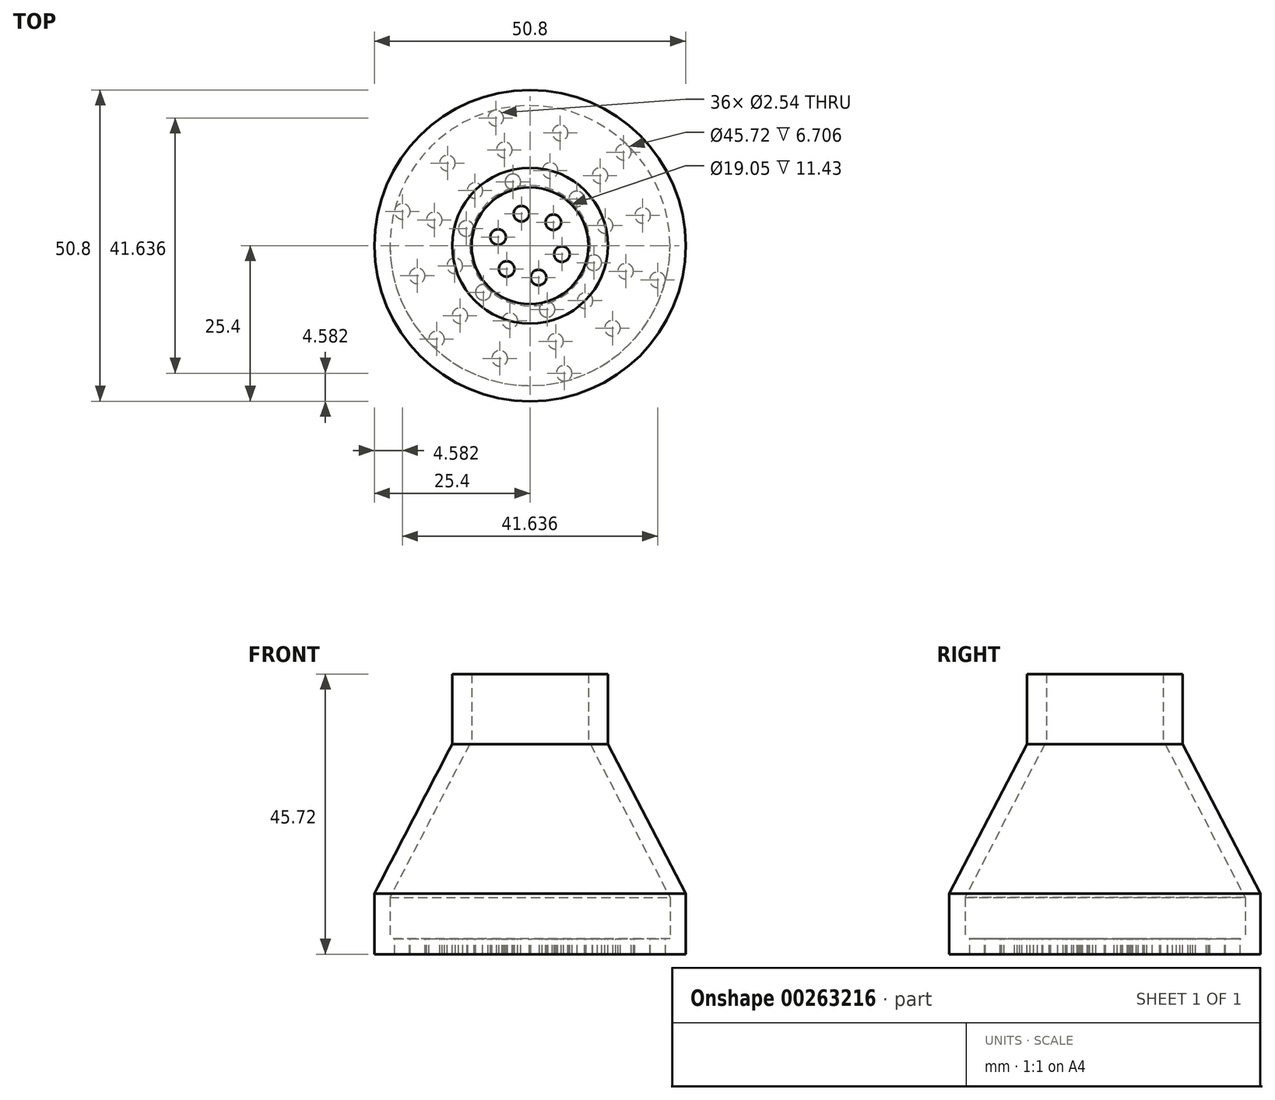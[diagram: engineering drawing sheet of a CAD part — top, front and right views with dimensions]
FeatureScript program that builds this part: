
annotation { "Feature Type Name" : "Feature", "Feature Type Description" : "" }
export const myFeature = defineFeature(function(context is Context, id is Id, definition is map)
    precondition{}
    {
        {
            var Q0;
            Q0=qCreatedBy(makeId("Top.planeOp"),FACE);
            var sketch = newSketch(context, id + "F0", { "sketchPlane" : qUnion([Q0])});
            skCircle(sketch, "E0", {"center": v(0, 0) * mm, "radius": 25.4 * mm});
            skSolve(sketch);
        }
        {
            var Q0;
            Q0 = qSketchRegion(id + "F0", true);
            var Q1;
            Q1=sQuery(id+"F0.wireOp",EDGE,"E0");
            extrude(context, id + "F1", {"entities" : qUnion([Q0]), "surfaceEntities" : qUnion([Q1]), "depth" : 31.75 * mm});
        }
        {
            var Q0;
            Q0=qCreatedBy(makeId("Right.planeOp"),FACE);
            var sketch = newSketch(context, id + "F2", { "sketchPlane" : qUnion([Q0])});
            skLineSegment(sketch, "E1", {"start": v(0, 0) * mm, "end": v(-29.21, 0) * mm, "construction": true});
            skLineSegment(sketch, "E2", {"start": v(-29.21, 0) * mm, "end": v(-12.7, 31.75) * mm});
            skLineSegment(sketch, "E3", {"start": v(-12.7, 31.75) * mm, "end": v(0, 31.75) * mm, "construction": true});
            skLineSegment(sketch, "E4", {"start": v(0, 31.75) * mm, "end": v(0, 0) * mm, "construction": true});
            skLineSegment(sketch, "E5", {"start": v(-29.21, 0) * mm, "end": v(-29.21, 31.75) * mm});
            skLineSegment(sketch, "E6", {"start": v(-29.21, 31.75) * mm, "end": v(-12.7, 31.75) * mm});
            skSolve(sketch);
        }
        {
            var Q0;
            Q0=makeQuery(id+"F2.imprint","IMPRINT",FACE,{"disambiguationData":[TD([[makeQuery(id+"F2.imprint","IMPRINT",EDGE,{"derivedFrom":sQuery(id+"F2.wireOp",EDGE,"E2")}),1.0]])]});
            var Q1;
            Q1=sQuery(id+"F2.wireOp",EDGE,"E4");
            revolve(context, id + "F3", {"operationType" : NewBodyOperationType.REMOVE, "entities" : qUnion([Q0]), "axis" : qUnion([Q1]), "revolveType" : RevolveType.FULL, "oppositeDirection" : true});
        }
        {
            var Q0;
            Q0=makeQuery(id+"F1.opExtrude","CAP_FACE",FACE,{"disambiguationData":[OSD([sQuery(id+"F0.wireOp",EDGE,"E0")])],"isStart":true});
            var Q1;
            Q1=makeQuery(id+"F1.opExtrude","CAP_FACE",FACE,{"disambiguationData":[OSD([sQuery(id+"F0.wireOp",EDGE,"E0")])],"isStart":false});
            shell(context, id + "F4", {"entities" : qUnion([Q0, Q1]), "thickness" : 2.54 * mm});
        }
        {
            var Q0;
            Q0=makeQuery(id+"F1.opExtrude","CAP_FACE",FACE,{"disambiguationData":[OSD([sQuery(id+"F0.wireOp",EDGE,"E0")])],"isStart":false});
            var sketch = newSketch(context, id + "F5", { "sketchPlane" : qUnion([Q0])});
            skCircle(sketch, "E7", {"center": v(0, 0) * mm, "radius": 12.7 * mm});
            skCircle(sketch, "E8", {"center": v(0, 0) * mm, "radius": 9.53 * mm});
            skSolve(sketch);
        }
        {
            var Q0;
            Q0 = qSketchRegion(id + "F5", true);
            extrude(context, id + "F6", {"entities" : qUnion([Q0]), "operationType" : NewBodyOperationType.ADD, "depth" : 11.43 * mm});
        }
        {
            var Q0;
            Q0=makeQuery(id+"F1.opExtrude","CAP_FACE",FACE,{"disambiguationData":[OSD([sQuery(id+"F0.wireOp",EDGE,"E0")])],"isStart":true});
            var sketch = newSketch(context, id + "F7", { "sketchPlane" : qUnion([Q0])});
            skCircle(sketch, "E9", {"center": v(0, 0) * mm, "radius": 25.4 * mm});
            skLineSegment(sketch, "E10.bottom", {"start": v(0, 0) * mm, "end": v(-3.8, 0) * mm, "construction": true});
            skLineSegment(sketch, "E10.top", {"start": v(0, 3.81) * mm, "end": v(-3.81, 3.8) * mm, "construction": true});
            skLineSegment(sketch, "E10.left", {"start": v(0, 0) * mm, "end": v(0, 3.81) * mm, "construction": true});
            skLineSegment(sketch, "E10.right", {"start": v(-3.8, 0) * mm, "end": v(-3.81, 3.8) * mm, "construction": true});
            skCircle(sketch, "E11", {"center": v(-3.81, 3.8) * mm, "radius": 1.27 * mm});
            skCircle(sketch, "E12.1.0", {"center": v(5.2, 1.4) * mm, "radius": 1.27 * mm});
            skCircle(sketch, "E12.2.0", {"center": v(-1.4, -5.2) * mm, "radius": 1.27 * mm});
            skLineSegment(sketch, "E12.anchor1", {"start": v(0, 0) * mm, "end": v(-3.81, 3.8) * mm, "construction": true});
            skLineSegment(sketch, "E12.anchor2", {"start": v(0, 0) * mm, "end": v(-1.4, -5.2) * mm, "construction": true});
            skLineSegment(sketch, "E13", {"start": v(0, 0) * mm, "end": v(5.2, 1.4) * mm, "construction": true});
            skLineSegment(sketch, "E14", {"start": v(0, 0) * mm, "end": v(1.4, 5.2) * mm, "construction": true});
            skCircle(sketch, "E15", {"center": v(1.4, 5.2) * mm, "radius": 1.27 * mm});
            skCircle(sketch, "E16.1.0", {"center": v(-5.2, -1.4) * mm, "radius": 1.27 * mm});
            skCircle(sketch, "E16.2.0", {"center": v(3.81, -3.8) * mm, "radius": 1.27 * mm});
            skLineSegment(sketch, "E17", {"start": v(-5.2, -1.4) * mm, "end": v(0, 0) * mm, "construction": true});
            skLineSegment(sketch, "E18", {"start": v(3.81, -3.8) * mm, "end": v(0, 0) * mm, "construction": true});
            skCircle(sketch, "E19", {"center": v(-7.62, 7.62) * mm, "radius": 1.27 * mm});
            skCircle(sketch, "E20.1.0", {"center": v(10.4, 2.79) * mm, "radius": 1.27 * mm});
            skCircle(sketch, "E20.2.0", {"center": v(-2.79, -10.4) * mm, "radius": 1.27 * mm});
            skLineSegment(sketch, "E20.anchor1", {"start": v(0, 0) * mm, "end": v(-7.62, 7.62) * mm, "construction": true});
            skLineSegment(sketch, "E20.anchor2", {"start": v(0, 0) * mm, "end": v(-2.79, -10.4) * mm, "construction": true});
            skLineSegment(sketch, "E21", {"start": v(0, 0) * mm, "end": v(10.4, 2.79) * mm, "construction": true});
            skLineSegment(sketch, "E22", {"start": v(0, 0) * mm, "end": v(2.79, 10.4) * mm, "construction": true});
            skCircle(sketch, "E23", {"center": v(2.79, 10.4) * mm, "radius": 1.27 * mm});
            skCircle(sketch, "E24.1.0", {"center": v(-10.4, -2.79) * mm, "radius": 1.27 * mm});
            skCircle(sketch, "E24.2.0", {"center": v(7.62, -7.62) * mm, "radius": 1.27 * mm});
            skLineSegment(sketch, "E25", {"start": v(-10.4, -2.79) * mm, "end": v(0, 0) * mm, "construction": true});
            skLineSegment(sketch, "E26", {"start": v(7.62, -7.62) * mm, "end": v(0, 0) * mm, "construction": true});
            skCircle(sketch, "E27", {"center": v(-15.24, 15.24) * mm, "radius": 1.27 * mm});
            skCircle(sketch, "E28.1.0", {"center": v(20.82, 5.58) * mm, "radius": 1.27 * mm});
            skCircle(sketch, "E28.2.0", {"center": v(-5.58, -20.82) * mm, "radius": 1.27 * mm});
            skLineSegment(sketch, "E28.anchor1", {"start": v(0, 0) * mm, "end": v(-15.24, 15.24) * mm, "construction": true});
            skLineSegment(sketch, "E28.anchor2", {"start": v(0, 0) * mm, "end": v(-5.58, -20.82) * mm, "construction": true});
            skLineSegment(sketch, "E29", {"start": v(0, 0) * mm, "end": v(20.82, 5.58) * mm, "construction": true});
            skLineSegment(sketch, "E30", {"start": v(0, 0) * mm, "end": v(5.58, 20.82) * mm, "construction": true});
            skCircle(sketch, "E31", {"center": v(5.58, 20.82) * mm, "radius": 1.27 * mm});
            skCircle(sketch, "E32.1.0", {"center": v(-20.82, -5.58) * mm, "radius": 1.27 * mm});
            skCircle(sketch, "E32.2.0", {"center": v(15.24, -15.24) * mm, "radius": 1.27 * mm});
            skLineSegment(sketch, "E33", {"start": v(-20.82, -5.58) * mm, "end": v(0, 0) * mm, "construction": true});
            skLineSegment(sketch, "E34", {"start": v(15.24, -15.24) * mm, "end": v(0, 0) * mm, "construction": true});
            skCircle(sketch, "E35", {"center": v(-11.43, 11.43) * mm, "radius": 1.27 * mm});
            skCircle(sketch, "E36.1.0", {"center": v(15.61, 4.18) * mm, "radius": 1.27 * mm});
            skCircle(sketch, "E36.2.0", {"center": v(-4.18, -15.61) * mm, "radius": 1.27 * mm});
            skLineSegment(sketch, "E36.anchor1", {"start": v(0, 0) * mm, "end": v(-11.43, 11.43) * mm, "construction": true});
            skLineSegment(sketch, "E36.anchor2", {"start": v(0, 0) * mm, "end": v(-4.18, -15.61) * mm, "construction": true});
            skLineSegment(sketch, "E37", {"start": v(0, 0) * mm, "end": v(15.61, 4.18) * mm, "construction": true});
            skLineSegment(sketch, "E38", {"start": v(0, 0) * mm, "end": v(4.18, 15.61) * mm, "construction": true});
            skCircle(sketch, "E39", {"center": v(4.18, 15.61) * mm, "radius": 1.27 * mm});
            skCircle(sketch, "E40.1.0", {"center": v(-15.61, -4.18) * mm, "radius": 1.27 * mm});
            skCircle(sketch, "E40.2.0", {"center": v(11.43, -11.43) * mm, "radius": 1.27 * mm});
            skLineSegment(sketch, "E41", {"start": v(-15.61, -4.18) * mm, "end": v(0, 0) * mm, "construction": true});
            skLineSegment(sketch, "E42", {"start": v(11.43, -11.43) * mm, "end": v(0, 0) * mm, "construction": true});
            skCircle(sketch, "E43", {"center": v(-18.4, 4.93) * mm, "radius": 1.27 * mm});
            skCircle(sketch, "E44.1.0", {"center": v(13.47, 13.47) * mm, "radius": 1.27 * mm});
            skCircle(sketch, "E44.2.0", {"center": v(4.93, -18.4) * mm, "radius": 1.27 * mm});
            skLineSegment(sketch, "E44.anchor1", {"start": v(0, 0) * mm, "end": v(-18.4, 4.93) * mm, "construction": true});
            skLineSegment(sketch, "E44.anchor2", {"start": v(0, 0) * mm, "end": v(4.93, -18.4) * mm, "construction": true});
            skLineSegment(sketch, "E45", {"start": v(0, 0) * mm, "end": v(13.47, 13.47) * mm, "construction": true});
            skLineSegment(sketch, "E46", {"start": v(0, 0) * mm, "end": v(-4.93, 18.4) * mm, "construction": true});
            skCircle(sketch, "E47", {"center": v(-4.93, 18.4) * mm, "radius": 1.27 * mm});
            skCircle(sketch, "E48.1.0", {"center": v(-13.47, -13.47) * mm, "radius": 1.27 * mm});
            skCircle(sketch, "E48.2.0", {"center": v(18.4, -4.93) * mm, "radius": 1.27 * mm});
            skLineSegment(sketch, "E49", {"start": v(-13.47, -13.47) * mm, "end": v(0, 0) * mm, "construction": true});
            skLineSegment(sketch, "E50", {"start": v(18.4, -4.93) * mm, "end": v(0, 0) * mm, "construction": true});
            skCircle(sketch, "E51", {"center": v(-12.27, 3.29) * mm, "radius": 1.27 * mm});
            skCircle(sketch, "E52.1.0", {"center": v(8.98, 8.98) * mm, "radius": 1.27 * mm});
            skCircle(sketch, "E52.2.0", {"center": v(3.29, -12.27) * mm, "radius": 1.27 * mm});
            skLineSegment(sketch, "E52.anchor1", {"start": v(0, 0) * mm, "end": v(-12.27, 3.29) * mm, "construction": true});
            skLineSegment(sketch, "E52.anchor2", {"start": v(0, 0) * mm, "end": v(3.29, -12.27) * mm, "construction": true});
            skLineSegment(sketch, "E53", {"start": v(0, 0) * mm, "end": v(8.98, 8.98) * mm, "construction": true});
            skLineSegment(sketch, "E54", {"start": v(0, 0) * mm, "end": v(-3.29, 12.27) * mm, "construction": true});
            skCircle(sketch, "E55", {"center": v(-3.29, 12.27) * mm, "radius": 1.27 * mm});
            skCircle(sketch, "E56.1.0", {"center": v(-8.98, -8.98) * mm, "radius": 1.27 * mm});
            skCircle(sketch, "E56.2.0", {"center": v(12.27, -3.29) * mm, "radius": 1.27 * mm});
            skLineSegment(sketch, "E57", {"start": v(-8.98, -8.98) * mm, "end": v(0, 0) * mm, "construction": true});
            skLineSegment(sketch, "E58", {"start": v(12.27, -3.29) * mm, "end": v(0, 0) * mm, "construction": true});
            skSolve(sketch);
        }
        {
            var Q0;
            Q0 = qSketchRegion(id + "F7", true);
            extrude(context, id + "F8", {"entities" : qUnion([Q0]), "operationType" : NewBodyOperationType.ADD, "depth" : 2.54 * mm});
        }
    });
